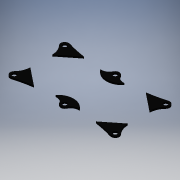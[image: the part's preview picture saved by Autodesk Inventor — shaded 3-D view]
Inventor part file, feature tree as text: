
AUTODESK INVENTOR PART (.ipt)
format: ipt  version: 2017 (Build 210142000, 142)  size: 228,864 bytes
history: native  units: mm (DEFAULTED — no unit token found)
features: fillet x4, extrude x3, sketch x3
ambient origin geometry x8: Origin, YZ Plane, XZ Plane, XY Plane, X Axis, Y Axis, Z Axis, Center Point
bodies: Solid1 (feature_tree)
feature tree (10):
  extrude  "Extrusion1"  Depth=24.0mm
  fillet  "Fillet3"  Radius=24.0mm
  fillet  "Fillet4"  Radius=24.0mm
  fillet  "Fillet5"  Radius=24.0mm
  fillet  "Fillet6"  Radius=24.0mm
  extrude  "Extrusion4"  Depth=24.0mm
  extrude  "Extrusion5"  Depth=12.0mm
  sketch  "Sketch1"  dims[d6=5.0mm d7=0.0mm d27=24.0mm d28=24.0mm d30=24.0mm d32=24.0mm d34=24.0mm]
  sketch  "Sketch6"  dims[d36=24.0mm d40=150.0mm]
  sketch  "Sketch7"  dims[d42=150.0mm d43=12.0mm d44=24.0mm d45=360.0mm d46=48.0mm d60=13.0mm d61=10.0mm d62=0.0mm d63=20.0mm d64=20.0mm d65=10.0mm d66=0.0mm]
